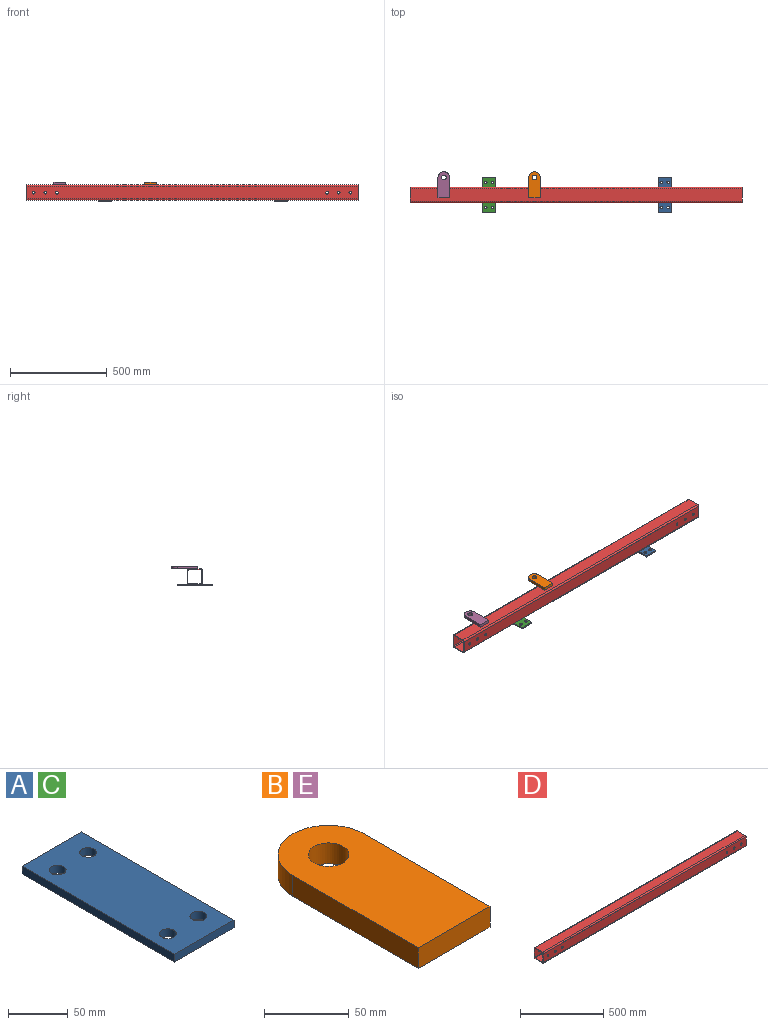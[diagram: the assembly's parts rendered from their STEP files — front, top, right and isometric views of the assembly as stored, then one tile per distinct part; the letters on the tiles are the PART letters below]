
ASSEMBLY  parts=5 mates=4
PART A: 10 faces, bbox 70x180x8 mm
  f0: plane 180x8mm, normal (-1,0,0), area 1440mm2, adj f1,f3,f4,f5
  f1: plane 70x8mm, normal (0,-1,0), area 560mm2, adj f0,f2,f4,f5
  f2: plane 180x8mm, normal (1,0,0), area 1440mm2, adj f1,f3,f4,f5
  f3: plane 70x8mm, normal (0,1,0), area 560mm2, adj f0,f2,f4,f5
  f4: plane 180x70mm, normal (0,0,-1), area 11984.2mm2, adj f0,f1,f2,f3,f6,f7,f8,f9
  f5: plane 180x70mm, normal (0,0,1), area 11984.2mm2, adj f0,f1,f2,f3,f6,f7,f8,f9
  f6: cylinder r=7mm len=14mm, axis (0,0,1), area 351.9mm2, adj f4,f5
  f7: cylinder r=7mm len=14mm, axis (0,0,1), area 351.9mm2, adj f4,f5
  f8: cylinder r=7mm len=14mm, axis (0,0,1), area 351.9mm2, adj f4,f5
  f9: cylinder r=7mm len=14mm, axis (0,0,1), area 351.9mm2, adj f4,f5
PART B: 7 faces, bbox 60x135x15 mm
  f0: plane 105x15mm, normal (-1,0,0), area 1575mm2, adj f1,f4,f5,f6
  f1: plane 60x15mm, normal (0,-1,0), area 900mm2, adj f0,f2,f5,f6
  f2: plane 105x15mm, normal (1,0,0), area 1575mm2, adj f1,f4,f5,f6
  f3: cylinder r=12mm len=24mm, axis (0,0,1), area 1131mm2, adj f5,f6
  f4: cylinder r=30mm len=60mm, axis (0,0,1), area 1413.7mm2, adj f0,f2,f5,f6
  f5: plane 135x60mm, normal (0,0,-1), area 7261.3mm2, adj f0,f1,f2,f3,f4
  f6: plane 135x60mm, normal (0,0,1), area 7261.3mm2, adj f0,f1,f2,f3,f4
PART C: same geometry as A
PART D: 30 faces, bbox 1720x80x80 mm
  f0: plane 80x80mm, normal (1,0,0), area 1174.8mm2, adj f2,f3,f4,f5,f6,f7,f8,f9
  f1: plane 80x80mm, normal (-1,0,0), area 1174.8mm2, adj f2,f3,f4,f5,f6,f7,f8,f9
  f2: plane 1720x64mm, normal (0,0,1), area 110080mm2, adj f0,f1,f3,f9
  f3: cylinder r=8mm len=1720mm, axis (-1,0,0), area 21614.2mm2, adj f0,f1,f2,f4
  f4: plane 1720x64mm, normal (0,-1,0), area 109156.4mm2, adj f0,f1,f3,f5,f24,f25,f26,f27
  f5: cylinder r=8mm len=1720mm, axis (-1,0,0), area 21614.2mm2, adj f0,f1,f4,f6
  f6: plane 1720x64mm, normal (0,0,-1), area 110080mm2, adj f0,f1,f5,f7
  f7: cylinder r=8mm len=1720mm, axis (-1,0,0), area 21614.2mm2, adj f0,f1,f6,f8
  f8: plane 1720x64mm, normal (0,1,0), area 109156.4mm2, adj f0,f1,f7,f9,f18,f19,f20,f21
  f9: cylinder r=8mm len=1720mm, axis (-1,0,0), area 21614.2mm2, adj f0,f1,f2,f8
  f10: plane 1720x64mm, normal (0,0,-1), area 110080mm2, adj f0,f1,f11,f17
  f11: cylinder r=4mm len=1720mm, axis (-1,0,0), area 10807.1mm2, adj f0,f1,f10,f12
  f12: plane 1720x64mm, normal (0,1,0), area 109156.4mm2, adj f0,f1,f11,f13,f24,f25,f26,f27
  f13: cylinder r=4mm len=1720mm, axis (-1,0,0), area 10807.1mm2, adj f0,f1,f12,f14
  f14: plane 1720x64mm, normal (0,0,1), area 110080mm2, adj f0,f1,f13,f15
  f15: cylinder r=4mm len=1720mm, axis (-1,0,0), area 10807.1mm2, adj f0,f1,f14,f16
  f16: plane 1720x64mm, normal (0,-1,0), area 109156.4mm2, adj f0,f1,f15,f17,f18,f19,f20,f21
  f17: cylinder r=4mm len=1720mm, axis (-1,0,0), area 10807.1mm2, adj f0,f1,f10,f16
  f18: cylinder r=7mm len=14mm, axis (0,-1,0), area 175.9mm2, adj f8,f16
  f19: cylinder r=7mm len=14mm, axis (0,-1,0), area 175.9mm2, adj f8,f16
  f20: cylinder r=7mm len=14mm, axis (0,-1,0), area 175.9mm2, adj f8,f16
  f21: cylinder r=7mm len=14mm, axis (0,-1,0), area 175.9mm2, adj f8,f16
  f22: cylinder r=7mm len=14mm, axis (0,-1,0), area 175.9mm2, adj f8,f16
  f23: cylinder r=7mm len=14mm, axis (0,-1,0), area 175.9mm2, adj f8,f16
  f24: cylinder r=7mm len=14mm, axis (0,-1,0), area 175.9mm2, adj f4,f12
  f25: cylinder r=7mm len=14mm, axis (0,-1,0), area 175.9mm2, adj f4,f12
  f26: cylinder r=7mm len=14mm, axis (0,-1,0), area 175.9mm2, adj f4,f12
  f27: cylinder r=7mm len=14mm, axis (0,-1,0), area 175.9mm2, adj f4,f12
  f28: cylinder r=7mm len=14mm, axis (0,-1,0), area 175.9mm2, adj f4,f12
  f29: cylinder r=7mm len=14mm, axis (0,-1,0), area 175.9mm2, adj f4,f12
PART E: same geometry as B
PLACE A t=(65.8,84.22,-67.31)mm
PLACE B t=(-604.2,159.22,27.69)mm
PLACE C t=(-844.2,84.22,-67.31)mm
PLACE D t=(-1219.2,134.22,-67.31)mm
PLACE E t=(-1074.2,159.22,27.69)mm
MATE fastened E.f5 <-> D.f2  axis (0,0,1) through (-1044.2,159.22,12.69)mm
MATE fastened B.f5 <-> D.f2  axis (0,0,1) through (-574.2,159.22,12.69)mm
MATE fastened C.f5 <-> D.f6  axis (0,0,1) through (-809.2,174.22,-67.31)mm
MATE fastened A.f5 <-> D.f6  axis (0,0,1) through (100.8,174.22,-67.31)mm
